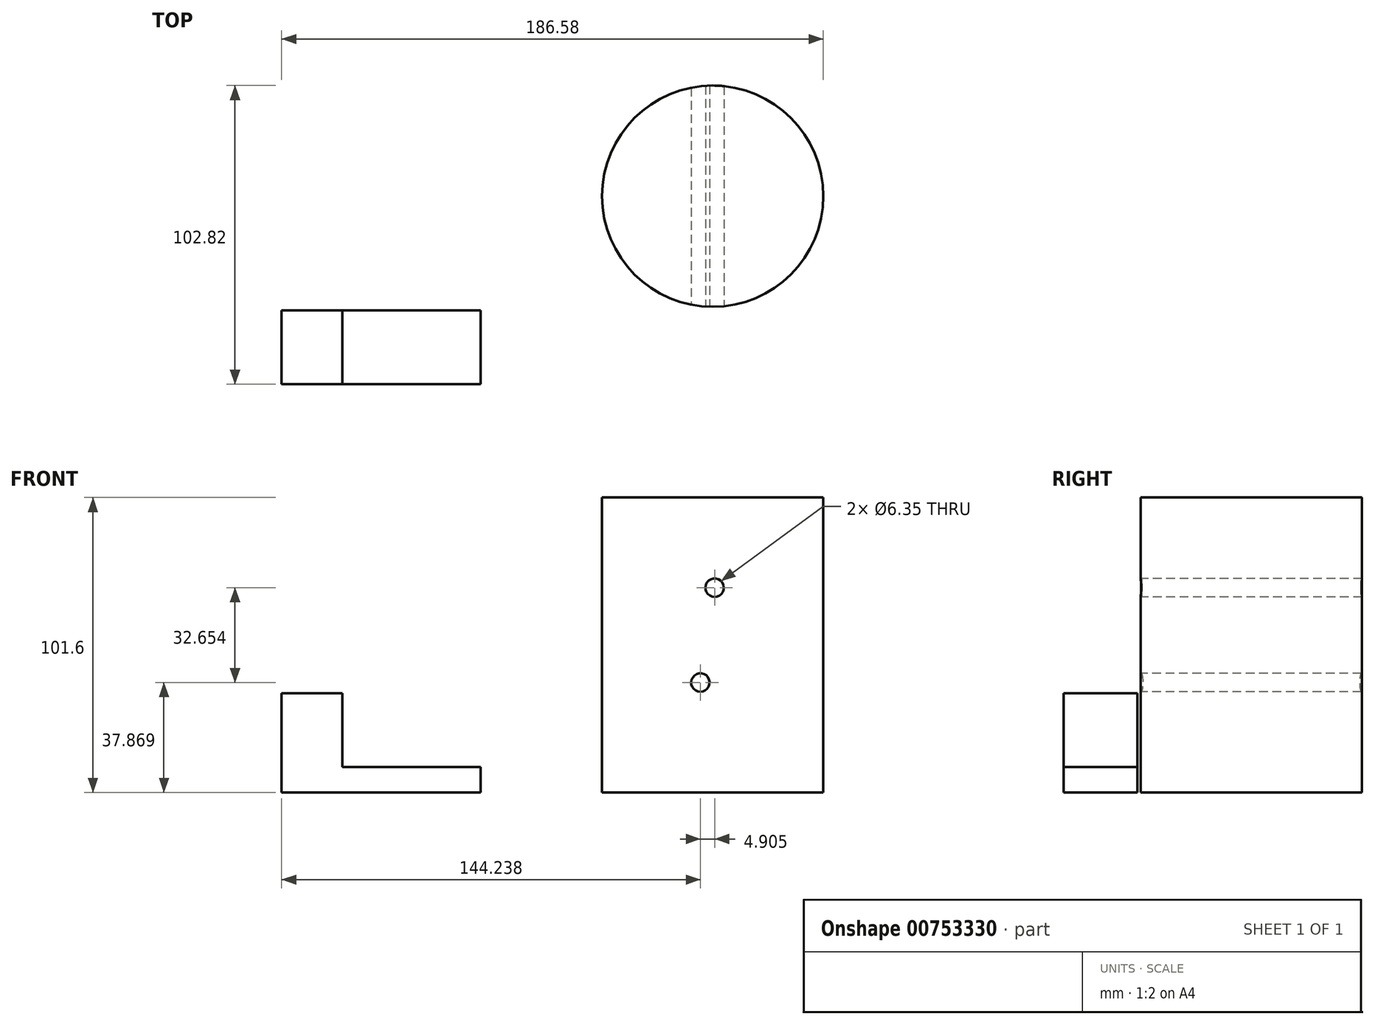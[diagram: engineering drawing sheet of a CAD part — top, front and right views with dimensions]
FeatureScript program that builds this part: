
annotation { "Feature Type Name" : "Feature", "Feature Type Description" : "" }
export const myFeature = defineFeature(function(context is Context, id is Id, definition is map)
    precondition{}
    {
        {
            var Q0;
            Q0=qCreatedBy(makeId("Front.planeOp"),FACE);
            var sketch = newSketch(context, id + "F0", { "sketchPlane" : qUnion([Q0])});
            skLineSegment(sketch, "E0.bottom", {"start": v(-68.58, 8.77) * mm, "end": v(0, 8.77) * mm});
            skLineSegment(sketch, "E0.top", {"start": v(-68.58, 0) * mm, "end": v(0, 0) * mm});
            skLineSegment(sketch, "E0.left", {"start": v(-68.58, 8.77) * mm, "end": v(-68.58, 0) * mm});
            skLineSegment(sketch, "E0.right", {"start": v(0, 8.77) * mm, "end": v(0, 0) * mm});
            skSolve(sketch);
        }
        {
            var Q0;
            Q0 = qSketchRegion(id + "F0", true);
            extrude(context, id + "F1", {"entities" : qUnion([Q0]), "depth" : 25.4 * mm, "offsetDistance" : 25.4 * mm});
        }
        {
            var Q0;
            Q0=makeQuery(id+"F1.opExtrude","SWEPT_FACE",FACE,{"disambiguationData":[OSD([sQuery(id+"F0.wireOp",EDGE,"E0.bottom")])]});
            var sketch = newSketch(context, id + "F2", { "sketchPlane" : qUnion([Q0])});
            skLineSegment(sketch, "E1", {"start": v(-47.66, 0) * mm, "end": v(-47.66, -25.4) * mm});
            skSolve(sketch);
        }
        {
            var Q0;
            {var subQ0=sQuery(id+"F2.wireOp",EDGE,"E1");Q0=makeQuery(id+"F2.imprint","IMPRINT",FACE,{"disambiguationData":[TD([[makeQuery(id+"F2.imprint","IMPRINT",EDGE,{"derivedFrom":subQ0}),-1.0]])]});}
            extrude(context, id + "F3", {"entities" : qUnion([Q0]), "operationType" : NewBodyOperationType.ADD, "depth" : 25.4 * mm, "offsetDistance" : 25.4 * mm});
        }
        {
            var Q0;
            Q0=qCreatedBy(makeId("Top.planeOp"),FACE);
            var sketch = newSketch(context, id + "F4", { "sketchPlane" : qUnion([Q0])});
            skCircle(sketch, "E2", {"center": v(79.9, 39.32) * mm, "radius": 38.1 * mm});
            skSolve(sketch);
        }
        {
            var Q0;
            Q0=makeQuery(id+"F4.imprint","IMPRINT",FACE,{"disambiguationData":[TD([[makeQuery(id+"F4.imprint","IMPRINT",EDGE,{"derivedFrom":sQuery(id+"F4.wireOp",EDGE,"E2")}),1.0]])]});
            extrude(context, id + "F5", {"entities" : qUnion([Q0]), "depth" : 101.6 * mm, "offsetDistance" : 25.4 * mm});
        }
        {
            var Q0;
            Q0=qCreatedBy(makeId("Front.planeOp"),FACE);
            var sketch = newSketch(context, id + "F6", { "sketchPlane" : qUnion([Q0])});
            skCircle(sketch, "E3", {"center": v(80.56, 70.52) * mm, "radius": 5.45 * mm});
            skSolve(sketch);
        }
        {
            var Q0;
            Q0=sQuery(id+"F6.wireOp",VERTEX,"E3.center");
            var Q1;
            Q1=makeQuery(id+"F5.opExtrude","SWEPT_BODY",BODY,{"disambiguationData":[OSD([sQuery(id+"F4.wireOp",EDGE,"E2")])]});
            hole(context, id + "F7", {"style" : HoleStyle.SIMPLE, "endStyle" : HoleEndStyle.THROUGH, "holeDiameter" : 6.35 * mm, "majorDiameter" : 6.35 * mm, "isTappedThrough" : true, "tappedDepth" : 12.7 * mm, "tapClearance" : 3, "locations" : qUnion([Q0]), "scope" : qUnion([Q1])});
        }
        {
            var Q0;
            Q0=qCreatedBy(makeId("Front.planeOp"),FACE);
            var sketch = newSketch(context, id + "F8", { "sketchPlane" : qUnion([Q0])});
            skPoint(sketch, "E4", {"position": v(75.66, 37.87) * mm});
            skSolve(sketch);
        }
        {
            var Q0;
            Q0=sQuery(id+"F8.wireOp",VERTEX,"E4");
            var Q1;
            Q1=makeQuery(id+"F5.opExtrude","SWEPT_BODY",BODY,{"disambiguationData":[OSD([sQuery(id+"F4.wireOp",EDGE,"E2")])]});
            hole(context, id + "F9", {"style" : HoleStyle.SIMPLE, "endStyle" : HoleEndStyle.THROUGH, "holeDiameter" : 6.35 * mm, "majorDiameter" : 6.35 * mm, "isTappedThrough" : true, "tappedDepth" : 12.7 * mm, "tapClearance" : 3, "locations" : qUnion([Q0]), "scope" : qUnion([Q1])});
        }
    });
